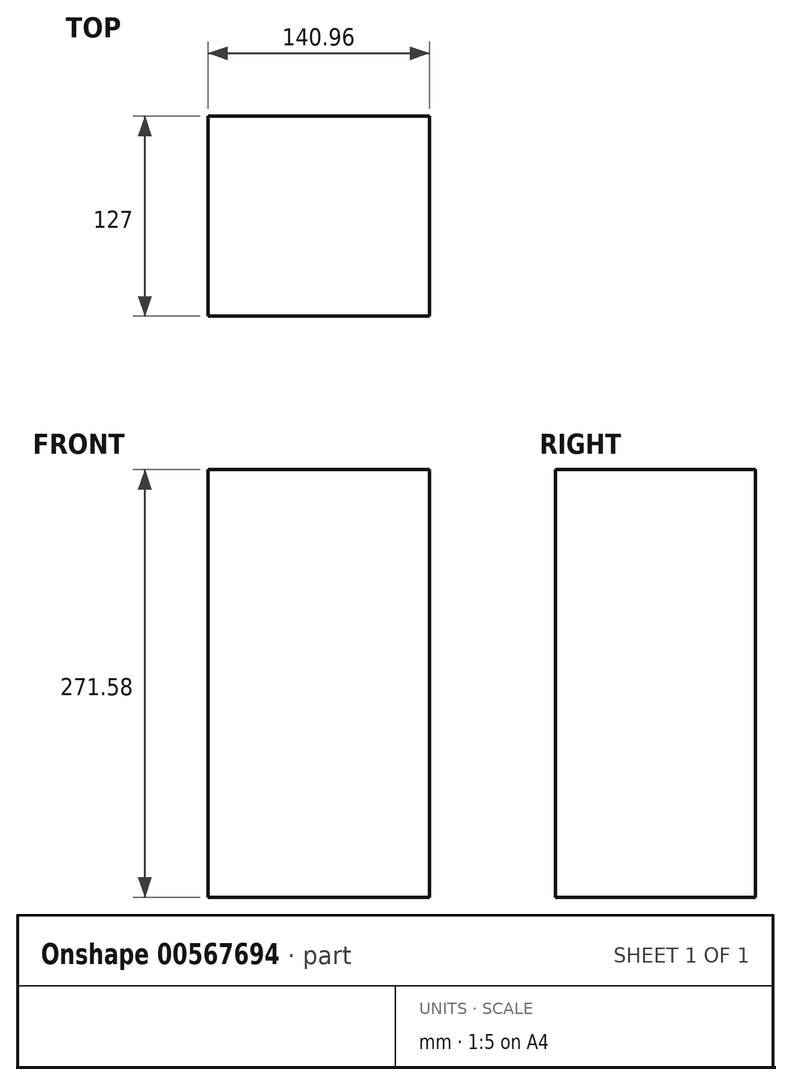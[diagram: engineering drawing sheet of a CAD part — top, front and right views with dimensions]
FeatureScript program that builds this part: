
annotation { "Feature Type Name" : "Feature", "Feature Type Description" : "" }
export const myFeature = defineFeature(function(context is Context, id is Id, definition is map)
    precondition{}
    {
        {
            var Q0;
            Q0=qCreatedBy(makeId("Front.planeOp"),FACE);
            var sketch = newSketch(context, id + "F0", { "sketchPlane" : qUnion([Q0])});
            skLineSegment(sketch, "E0.bottom", {"start": v(70.48, -86.6) * mm, "end": v(-70.48, -86.6) * mm});
            skLineSegment(sketch, "E0.top", {"start": v(70.48, 159.58) * mm, "end": v(-70.48, 159.58) * mm});
            skLineSegment(sketch, "E0.left", {"start": v(70.48, -86.6) * mm, "end": v(70.48, 159.58) * mm});
            skLineSegment(sketch, "E0.right", {"start": v(-70.48, -86.6) * mm, "end": v(-70.48, 159.58) * mm});
            skPoint(sketch, "E0.middle", {"position": v(0, 36.5) * mm});
            skSolve(sketch);
        }
        {
            var Q0;
            Q0 = qSketchRegion(id + "F0", true);
            extrude(context, id + "F1", {"entities" : qUnion([Q0]), "depth" : 127 * mm, "offsetDistance" : 25.4 * mm});
        }
        {
            var Q0;
            Q0=makeQuery(id+"F1.opExtrude","SWEPT_FACE",FACE,{"disambiguationData":[OSD([sQuery(id+"F0.wireOp",EDGE,"E0.right")])]});
            var sketch = newSketch(context, id + "F2", { "sketchPlane" : qUnion([Q0])});
            skCircle(sketch, "E1", {"center": v(53.07, 72.76) * mm, "radius": 28.77 * mm});
            skSolve(sketch);
        }
        {
            var Q0;
            Q0=makeQuery(id+"F1.opExtrude","SWEPT_FACE",FACE,{"disambiguationData":[OSD([sQuery(id+"F0.wireOp",EDGE,"E0.top")])]});
            var Q1;
            Q1 = qSketchRegion(id + "F2", true);
            var Q2;
            Q2=sQuery(id+"F2.wireOp",EDGE,"E1");
            extrude(context, id + "F3", {"entities" : qUnion([Q0]), "operationType" : NewBodyOperationType.ADD, "surfaceEntities" : qUnion([Q1, Q2]), "depth" : 25.4 * mm, "offsetDistance" : 25.4 * mm});
        }
    });
